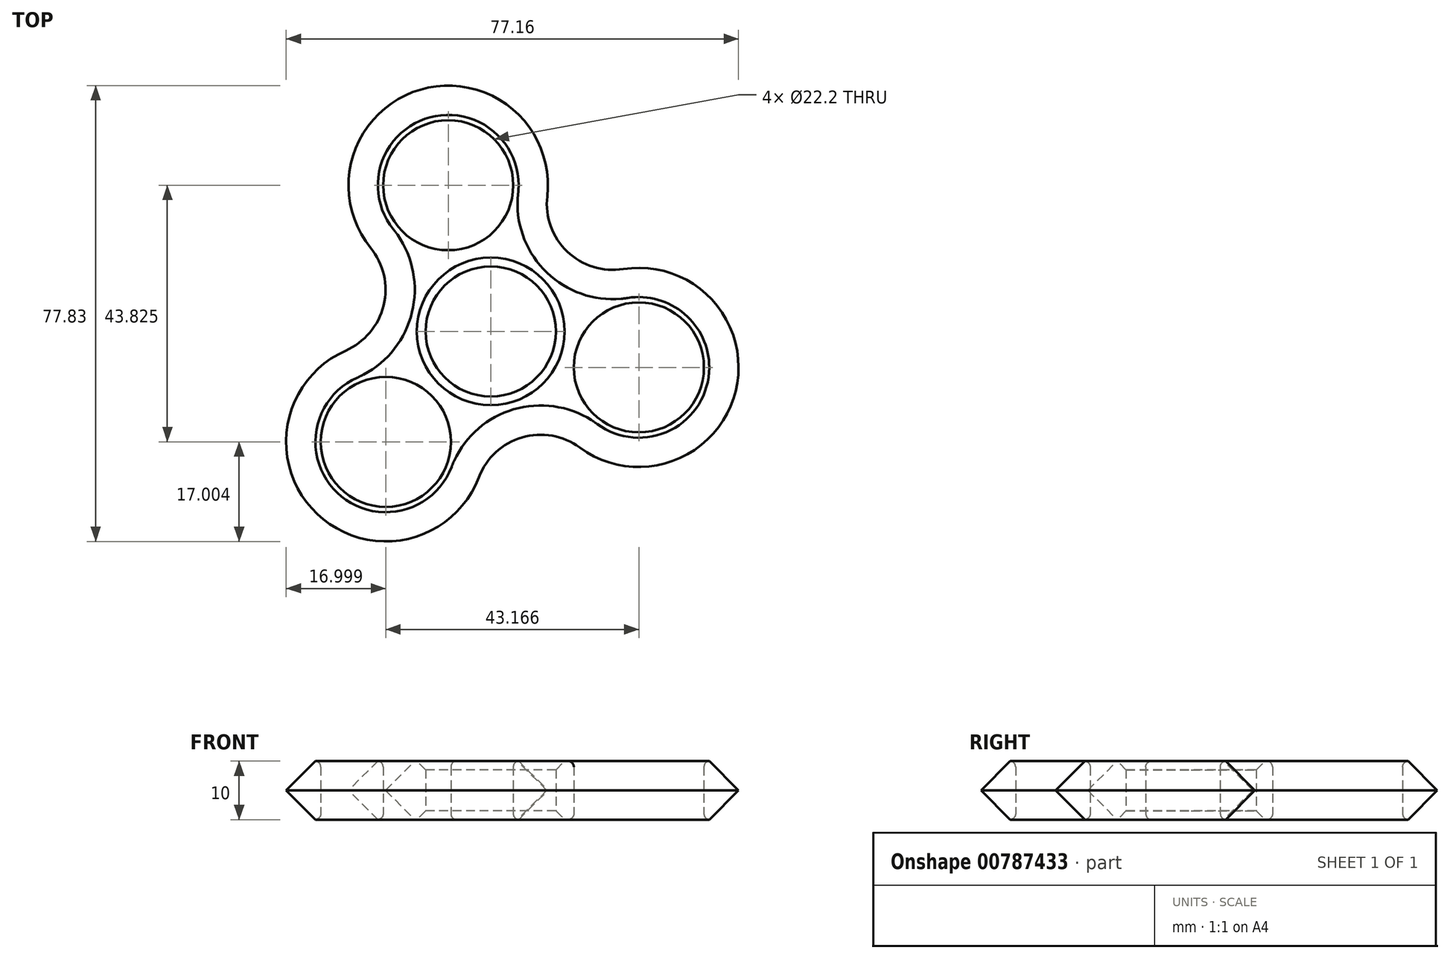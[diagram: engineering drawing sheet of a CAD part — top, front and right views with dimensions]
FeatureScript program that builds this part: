
annotation { "Feature Type Name" : "Feature", "Feature Type Description" : "" }
export const myFeature = defineFeature(function(context is Context, id is Id, definition is map)
    precondition{}
    {
        {
            var Q0;
            Q0=qCreatedBy(makeId("Top.planeOp"),FACE);
            var sketch = newSketch(context, id + "F0", { "sketchPlane" : qUnion([Q0])});
            skCircle(sketch, "E0", {"center": v(0, 0) * mm, "radius": 11.1 * mm});
            skCircle(sketch, "E1", {"center": v(-7.25, 24.97) * mm, "radius": 11.1 * mm});
            skCircle(sketch, "E2", {"center": v(25.26, -6.14) * mm, "radius": 11.1 * mm});
            skCircle(sketch, "E3", {"center": v(-17.9, -18.86) * mm, "radius": 11.1 * mm});
            skCircle(sketch, "E4", {"center": v(-17.9, -18.86) * mm, "radius": 17 * mm});
            skCircle(sketch, "E5", {"center": v(25.26, -6.14) * mm, "radius": 17 * mm});
            skCircle(sketch, "E6", {"center": v(-7.25, 24.97) * mm, "radius": 17 * mm});
            skArc(sketch, "E7", {"start": v(15.2, -19.83) * mm, "mid": v(5.33, -18.1) * mm, "end": v(-2.01, -24.9) * mm});
            skArc(sketch, "E8", {"start": v(9.64, 23.05) * mm, "mid": v(13.04, 13.64) * mm, "end": v(22.6, 10.65) * mm});
            skArc(sketch, "E9", {"start": v(-24.76, -3.3) * mm, "mid": v(-18.28, 4.44) * mm, "end": v(-20.49, 14.3) * mm});
            skCircle(sketch, "E10", {"center": v(0, 0) * mm, "radius": 12 * mm});
            skSolve(sketch);
        }
        {
            var Q0;
            Q0=makeQuery(id+"F0.imprint","IMPRINT",FACE,{"disambiguationData":[TD([[makeQuery(id+"F0.imprint","IMPRINT",EDGE,{"derivedFrom":sQuery(id+"F0.wireOp",EDGE,"E1")}),-1.0]])]});
            var Q1;
            {var subQ5=sQuery(id+"F0.wireOp",EDGE,"E8");Q1=makeQuery(id+"F0.imprint","IMPRINT",FACE,{"disambiguationData":[TD([[makeQuery(id+"F0.imprint","IMPRINT",EDGE,{"derivedFrom":subQ5}),-1.0]])]});}
            var Q2;
            Q2=makeQuery(id+"F0.imprint","IMPRINT",FACE,{"disambiguationData":[TD([[makeQuery(id+"F0.imprint","IMPRINT",EDGE,{"derivedFrom":sQuery(id+"F0.wireOp",EDGE,"E2")}),-1.0]])]});
            var Q3;
            {var subQ5=sQuery(id+"F0.wireOp",EDGE,"E7");Q3=makeQuery(id+"F0.imprint","IMPRINT",FACE,{"disambiguationData":[TD([[makeQuery(id+"F0.imprint","IMPRINT",EDGE,{"derivedFrom":subQ5}),-1.0]])]});}
            var Q4;
            Q4=makeQuery(id+"F0.imprint","IMPRINT",FACE,{"disambiguationData":[TD([[makeQuery(id+"F0.imprint","IMPRINT",EDGE,{"derivedFrom":sQuery(id+"F0.wireOp",EDGE,"E3")}),-1.0]])]});
            var Q5;
            {var subQ5=sQuery(id+"F0.wireOp",EDGE,"E9");Q5=makeQuery(id+"F0.imprint","IMPRINT",FACE,{"disambiguationData":[TD([[makeQuery(id+"F0.imprint","IMPRINT",EDGE,{"derivedFrom":subQ5}),-1.0]])]});}
            var Q6;
            {var subQ0=sQuery(id+"F0.wireOp",EDGE,"E6");var subQ1=sQuery(id+"F0.wireOp",EDGE,"E0");var subQ2=makeQuery(id+"F0.imprint","INTERSECT",VERTEX,{"disambiguationData":[OD(0.0)],"derivedFrom":[subQ1,subQ0]});Q6=makeQuery(id+"F0.imprint","IMPRINT",FACE,{"disambiguationData":[TD([[makeQuery(id+"F0.imprint","IMPRINT",EDGE,{"disambiguationData":[TD([[subQ2,-1.0]])],"derivedFrom":subQ1}),-1.0]])]});}
            var Q7;
            {var subQ0=sQuery(id+"F0.wireOp",EDGE,"E6");var subQ1=sQuery(id+"F0.wireOp",EDGE,"E0");var subQ2=makeQuery(id+"F0.imprint","INTERSECT",VERTEX,{"disambiguationData":[OD(1.0)],"derivedFrom":[subQ1,subQ0]});Q7=makeQuery(id+"F0.imprint","IMPRINT",FACE,{"disambiguationData":[TD([[makeQuery(id+"F0.imprint","IMPRINT",EDGE,{"disambiguationData":[TD([[subQ2,-1.0]])],"derivedFrom":subQ1}),-1.0]])]});}
            var Q8;
            {var subQ0=sQuery(id+"F0.wireOp",EDGE,"E6");var subQ1=sQuery(id+"F0.wireOp",EDGE,"E0");var subQ2=makeQuery(id+"F0.imprint","INTERSECT",VERTEX,{"disambiguationData":[OD(0.0)],"derivedFrom":[subQ1,subQ0]});Q8=makeQuery(id+"F0.imprint","IMPRINT",FACE,{"disambiguationData":[TD([[makeQuery(id+"F0.imprint","IMPRINT",EDGE,{"disambiguationData":[TD([[subQ2,1.0]])],"derivedFrom":subQ1}),-1.0]])]});}
            var Q9;
            {var subQ0=sQuery(id+"F0.wireOp",EDGE,"E5");var subQ1=sQuery(id+"F0.wireOp",EDGE,"E0");var subQ2=makeQuery(id+"F0.imprint","INTERSECT",VERTEX,{"disambiguationData":[OD(0.0)],"derivedFrom":[subQ1,subQ0]});Q9=makeQuery(id+"F0.imprint","IMPRINT",FACE,{"disambiguationData":[TD([[makeQuery(id+"F0.imprint","IMPRINT",EDGE,{"disambiguationData":[TD([[subQ2,1.0]])],"derivedFrom":subQ1}),-1.0]])]});}
            var Q10;
            {var subQ0=sQuery(id+"F0.wireOp",EDGE,"E4");var subQ1=sQuery(id+"F0.wireOp",EDGE,"E0");var subQ2=makeQuery(id+"F0.imprint","INTERSECT",VERTEX,{"disambiguationData":[OD(1.0)],"derivedFrom":[subQ1,subQ0]});Q10=makeQuery(id+"F0.imprint","IMPRINT",FACE,{"disambiguationData":[TD([[makeQuery(id+"F0.imprint","IMPRINT",EDGE,{"disambiguationData":[TD([[subQ2,-1.0]])],"derivedFrom":subQ1}),-1.0]])]});}
            var Q11;
            {var subQ0=sQuery(id+"F0.wireOp",EDGE,"E4");var subQ1=sQuery(id+"F0.wireOp",EDGE,"E0");var subQ2=makeQuery(id+"F0.imprint","INTERSECT",VERTEX,{"disambiguationData":[OD(0.0)],"derivedFrom":[subQ1,subQ0]});Q11=makeQuery(id+"F0.imprint","IMPRINT",FACE,{"disambiguationData":[TD([[makeQuery(id+"F0.imprint","IMPRINT",EDGE,{"disambiguationData":[TD([[subQ2,-1.0]])],"derivedFrom":subQ1}),-1.0]])]});}
            extrude(context, id + "F1", {"entities" : qUnion([Q0, Q1, Q2, Q3, Q4, Q5, Q6, Q7, Q8, Q9, Q10, Q11]), "depth" : 10 * mm, "offsetDistance" : 25 * mm});
        }
        {
            var Q0;
            Q0=makeQuery(id+"F1.opExtrude","CAP_EDGE",EDGE,{"disambiguationData":[OSD([sQuery(id+"F0.wireOp",EDGE,"E4")])],"isStart":false});
            var Q1;
            Q1=makeQuery(id+"F1.opExtrude","CAP_EDGE",EDGE,{"disambiguationData":[OSD([sQuery(id+"F0.wireOp",EDGE,"E5")])],"isStart":true});
            chamfer(context, id + "F2", {"entities" : qUnion([Q0, Q1]), "width" : 5 * mm, "tangentPropagation" : true});
        }
        {
            var Q0;
            Q0=makeQuery(id+"F1.opExtrude","CAP_EDGE",EDGE,{"disambiguationData":[OSD([sQuery(id+"F0.wireOp",EDGE,"E2")])],"isStart":false});
            var Q1;
            Q1=makeQuery(id+"F1.opExtrude","CAP_EDGE",EDGE,{"disambiguationData":[OSD([sQuery(id+"F0.wireOp",EDGE,"E1")])],"isStart":false});
            var Q2;
            Q2=makeQuery(id+"F1.opExtrude","CAP_EDGE",EDGE,{"disambiguationData":[OSD([sQuery(id+"F0.wireOp",EDGE,"E3")])],"isStart":false});
            var Q3;
            Q3=makeQuery(id+"F1.opExtrude","CAP_EDGE",EDGE,{"disambiguationData":[OSD([sQuery(id+"F0.wireOp",EDGE,"E2")])],"isStart":true});
            var Q4;
            Q4=makeQuery(id+"F1.opExtrude","CAP_EDGE",EDGE,{"disambiguationData":[OSD([sQuery(id+"F0.wireOp",EDGE,"E1")])],"isStart":true});
            var Q5;
            Q5=makeQuery(id+"F1.opExtrude","CAP_EDGE",EDGE,{"disambiguationData":[OSD([sQuery(id+"F0.wireOp",EDGE,"E3")])],"isStart":true});
            fillet(context, id + "F3", {"entities" : qUnion([Q0, Q1, Q2, Q3, Q4, Q5]), "radius" : 1 * mm, "tangentPropagation" : true, "allowEdgeOverflow" : false});
        }
        {
            var Q0;
            Q0=makeQuery(id+"F1.opExtrude","CAP_EDGE",EDGE,{"disambiguationData":[OSD([sQuery(id+"F0.wireOp",EDGE,"E0")])],"isStart":true});
            var Q1;
            Q1=makeQuery(id+"F1.opExtrude","SWEPT_FACE",FACE,{"disambiguationData":[OSD([sQuery(id+"F0.wireOp",EDGE,"E0")])]});
            chamfer(context, id + "F4", {"entities" : qUnion([Q0, Q1]), "width" : 1.5 * mm, "tangentPropagation" : true});
        }
    });
